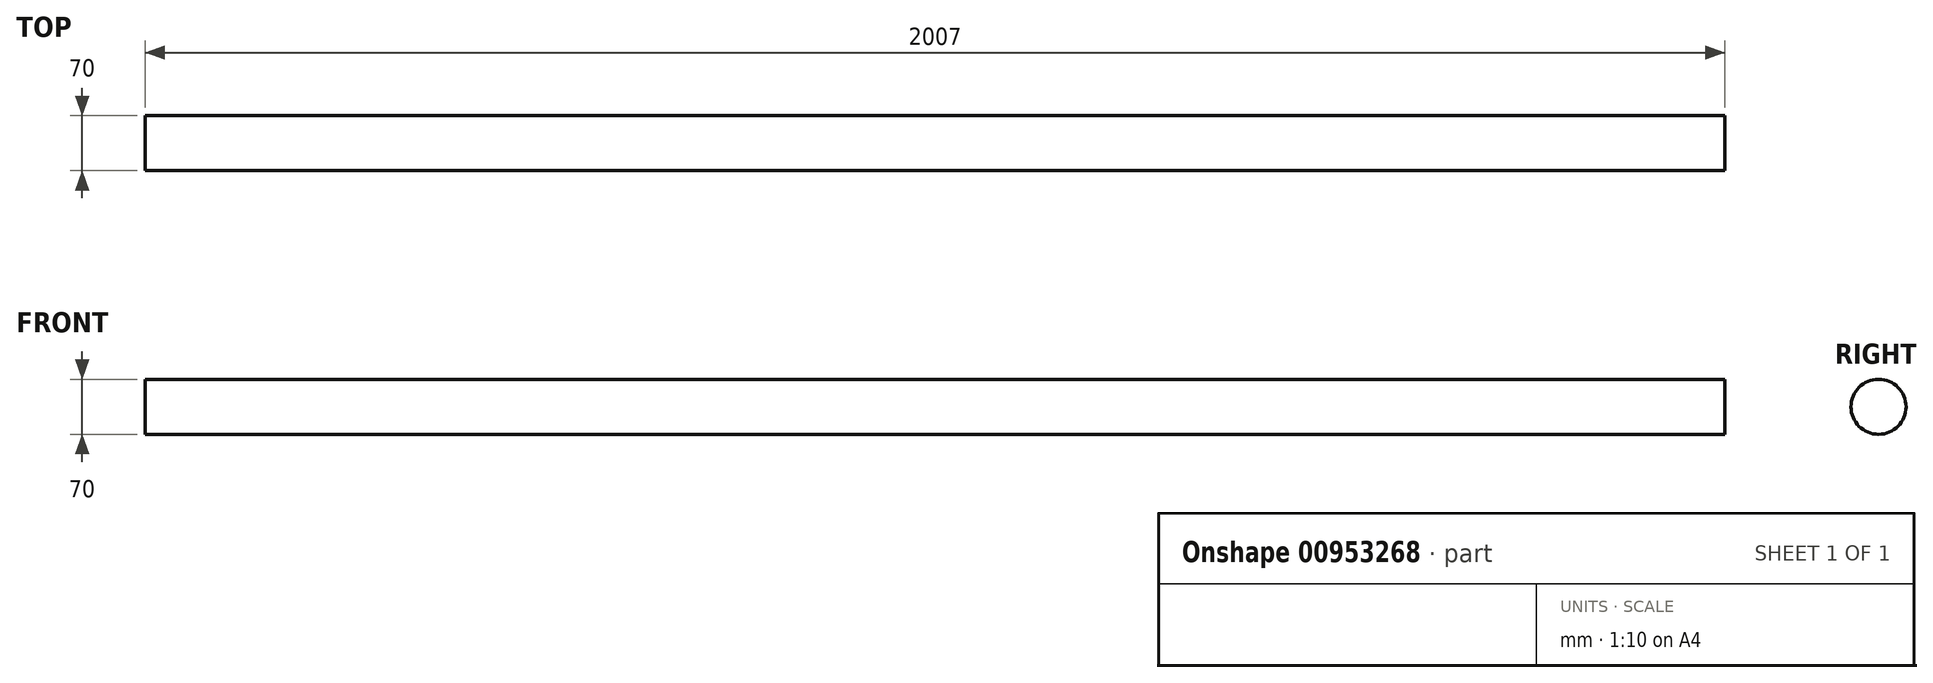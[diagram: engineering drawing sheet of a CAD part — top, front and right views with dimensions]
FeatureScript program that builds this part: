
annotation { "Feature Type Name" : "Feature", "Feature Type Description" : "" }
export const myFeature = defineFeature(function(context is Context, id is Id, definition is map)
    precondition{}
    {
        {
            var Q0;
            Q0=qCreatedBy(makeId("Right.planeOp"),FACE);
            var sketch = newSketch(context, id + "F0", { "sketchPlane" : qUnion([Q0])});
            skCircle(sketch, "E0", {"center": v(0, 0) * mm, "radius": 35 * mm});
            skSolve(sketch);
        }
        {
            var Q0;
            Q0=makeQuery(id+"F0.imprint","IMPRINT",FACE,{"disambiguationData":[TD([[makeQuery(id+"F0.imprint","IMPRINT",EDGE,{"derivedFrom":sQuery(id+"F0.wireOp",EDGE,"E0")}),1.0]])]});
            extrude(context, id + "F1", {"entities" : qUnion([Q0]), "oppositeDirection" : true, "depth" : 2007 * mm, "offsetDistance" : 25 * mm});
        }
        {
            var Q0;
            Q0=qCreatedBy(makeId("Right.planeOp"),FACE);
            cPlane(context, id + "F2", {"entities" : qUnion([Q0]), "cplaneType" : CPlaneType.OFFSET, "offset" : 350 * mm, "oppositeDirection" : true, "width" : 150 * mm, "height" : 150 * mm});
        }
    });
